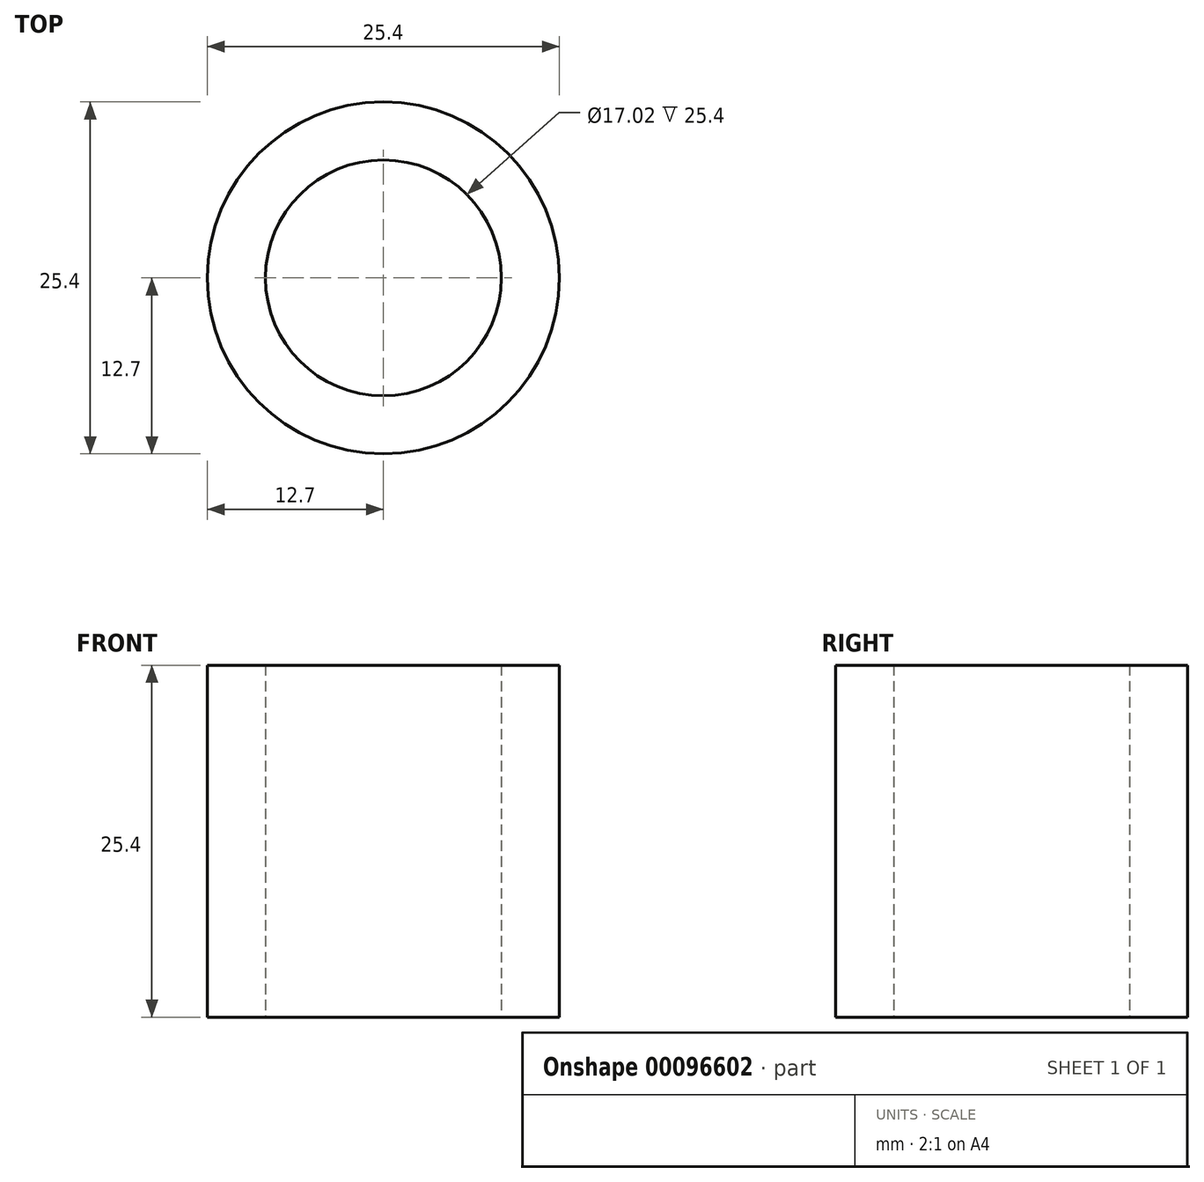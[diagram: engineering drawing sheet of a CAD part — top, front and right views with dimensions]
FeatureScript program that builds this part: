
annotation { "Feature Type Name" : "Feature", "Feature Type Description" : "" }
export const myFeature = defineFeature(function(context is Context, id is Id, definition is map)
    precondition{}
    {
        {
            var Q0;
            Q0=qCreatedBy(makeId("Top.planeOp"),FACE);
            var sketch = newSketch(context, id + "F0", { "sketchPlane" : qUnion([Q0])});
            skCircle(sketch, "E0", {"center": v(0, 0) * mm, "radius": 12.7 * mm});
            skCircle(sketch, "E1", {"center": v(0, 0) * mm, "radius": 8.5 * mm});
            skSolve(sketch);
        }
        {
            var Q0;
            Q0 = qSketchRegion(id + "F0", true);
            extrude(context, id + "F1", {"entities" : qUnion([Q0]), "depth" : 25.4 * mm, "offsetDistance" : 25.4 * mm});
        }
    });
